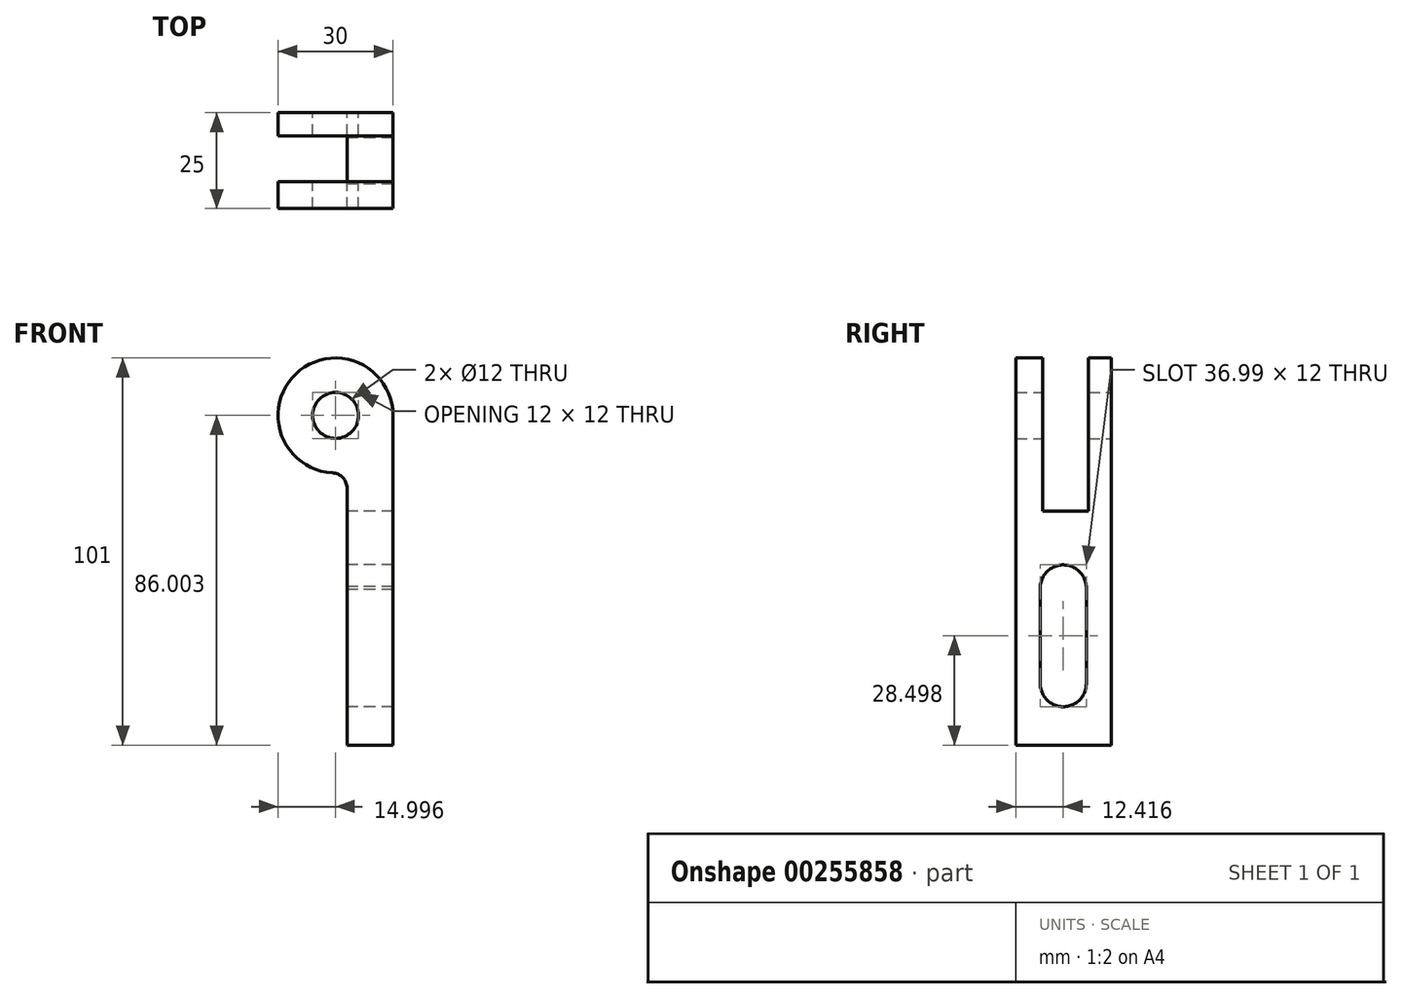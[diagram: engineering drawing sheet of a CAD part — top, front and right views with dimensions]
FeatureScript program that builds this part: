
annotation { "Feature Type Name" : "Feature", "Feature Type Description" : "" }
export const myFeature = defineFeature(function(context is Context, id is Id, definition is map)
    precondition{}
    {
        {
            var Q0;
            Q0=qCreatedBy(makeId("Front.planeOp"),FACE);
            var sketch = newSketch(context, id + "F0", { "sketchPlane" : qUnion([Q0])});
            skCircle(sketch, "E0", {"center": v(-13.41, 19.52) * mm, "radius": 6 * mm});
            skArc(sketch, "E1", {"start": v(1.59, 19.52) * mm, "mid": v(-23.74, 30.4) * mm, "end": v(-14.2, 4.54) * mm});
            skLineSegment(sketch, "E2.top", {"start": v(-10.41, -66.48) * mm, "end": v(1.59, -66.48) * mm});
            skLineSegment(sketch, "E2.right", {"start": v(1.59, 19.52) * mm, "end": v(1.59, -66.48) * mm});
            skLineSegment(sketch, "E3.trimOffspring", {"start": v(-10.41, 0.55) * mm, "end": v(-10.41, -66.48) * mm});
            skPoint(sketch, "E4.visualSharp", {"position": v(-10.41, 4.83) * mm});
            skArc(sketch, "E4.filletArc", {"start": v(-10.41, 0.55) * mm, "mid": v(-11.51, 3.3) * mm, "end": v(-14.2, 4.54) * mm});
            skSolve(sketch);
        }
        {
            var Q0;
            Q0=makeQuery(id+"F0.imprint","IMPRINT",FACE,{"disambiguationData":[TD([[makeQuery(id+"F0.imprint","IMPRINT",EDGE,{"derivedFrom":sQuery(id+"F0.wireOp",EDGE,"E0")}),-1.0]])]});
            extrude(context, id + "F1", {"entities" : qUnion([Q0]), "depth" : 25 * mm});
        }
        {
            var Q0;
            Q0=qCreatedBy(makeId("Right.planeOp"),FACE);
            cPlane(context, id + "F2", {"entities" : qUnion([Q0]), "cplaneType" : CPlaneType.OFFSET, "offset" : 58.7 * mm, "oppositeDirection" : true, "width" : 150 * mm, "height" : 150 * mm});
        }
        {
            var Q0;
            Q0=qCreatedBy(id+"F2.planeOp",FACE);
            var sketch = newSketch(context, id + "F3", { "sketchPlane" : qUnion([Q0])});
            skArc(sketch, "E5", {"start": v(-6.6, -25.76) * mm, "mid": v(-12.64, -19.48) * mm, "end": v(-18.57, -25.87) * mm});
            skArc(sketch, "E6", {"start": v(-18.58, -50.47) * mm, "mid": v(-12.58, -56.48) * mm, "end": v(-6.58, -50.48) * mm});
            skLineSegment(sketch, "E7", {"start": v(-6.6, -25.2) * mm, "end": v(-6.58, -50.48) * mm});
            skLineSegment(sketch, "E8", {"start": v(-18.57, -25.87) * mm, "end": v(-18.58, -50.47) * mm});
            skLineSegment(sketch, "E9.bottom", {"start": v(-6, 42.43) * mm, "end": v(-18, 42.43) * mm});
            skLineSegment(sketch, "E9.top", {"start": v(-6, -5.48) * mm, "end": v(-18, -5.48) * mm});
            skLineSegment(sketch, "E9.left", {"start": v(-6, 42.43) * mm, "end": v(-6, -5.48) * mm});
            skLineSegment(sketch, "E9.right", {"start": v(-18, 42.43) * mm, "end": v(-18, -5.48) * mm});
            skSolve(sketch);
        }
        {
            var Q0;
            Q0=makeQuery(id+"F3.imprint","IMPRINT",FACE,{"disambiguationData":[TD([[makeQuery(id+"F3.imprint","IMPRINT",EDGE,{"derivedFrom":sQuery(id+"F3.wireOp",EDGE,"E9.bottom")}),1.0]])]});
            var Q1;
            {var subQ4=sQuery(id+"F3.wireOp",EDGE,"E6");Q1=makeQuery(id+"F3.imprint","IMPRINT",FACE,{"disambiguationData":[TD([[makeQuery(id+"F3.imprint","IMPRINT",EDGE,{"derivedFrom":subQ4}),1.0]])]});}
            extrude(context, id + "F4", {"entities" : qUnion([Q0, Q1]), "operationType" : NewBodyOperationType.REMOVE, "endBound" : BoundingType.THROUGH_ALL, "depth" : 25 * mm});
        }
    });
